# Revit family: UHWD524-SG51A
name_source: partatom
category: Specialty Equipment
revit_build: Autodesk Revit 2017 (Build: 20160225_1515(x64)
units: mm (PartAtom-declared; Revit-internal decimal feet)

## family parameters
Always vertical = Yes
Cut with Voids When Loaded = No
Part Type = Normal
Room Calculation Point = No
Round Connector Dimension = Use Diameter
Shared = No
Work Plane-Based = No

## types (1)
- UHWD524-SG51A
    Depth = 22 15/16"
    Description = Field reversible door is shipped right-hand hinged
    Door Swing = Left-Hand Hinged
    Features and specifications = Convection colling system provides a quick cool down and consistent temperature
    Finish = Stainless Frame
    Height = 33 11/16"
    Lock = Yes
    Manufacturer = U-LINE
    Model = UHWD524-SG51A
    Pump = No
    Temperature range = 38 F - 65 F
    Type Comments = Volume of 5.1 cu ft holds up to 49 wine bottles (750 ml)
    U-Adjust interior = 17 possible positions
    URL = https://www.yepsketch.com
    Voltage/Hz = 115 v / 60 hz
    Width = 23 5/8"
    shipping weight = 159 lb

## geometry (parser evidence)
native form markers: Sweep x2
no freeform markers — native parametric forms only
